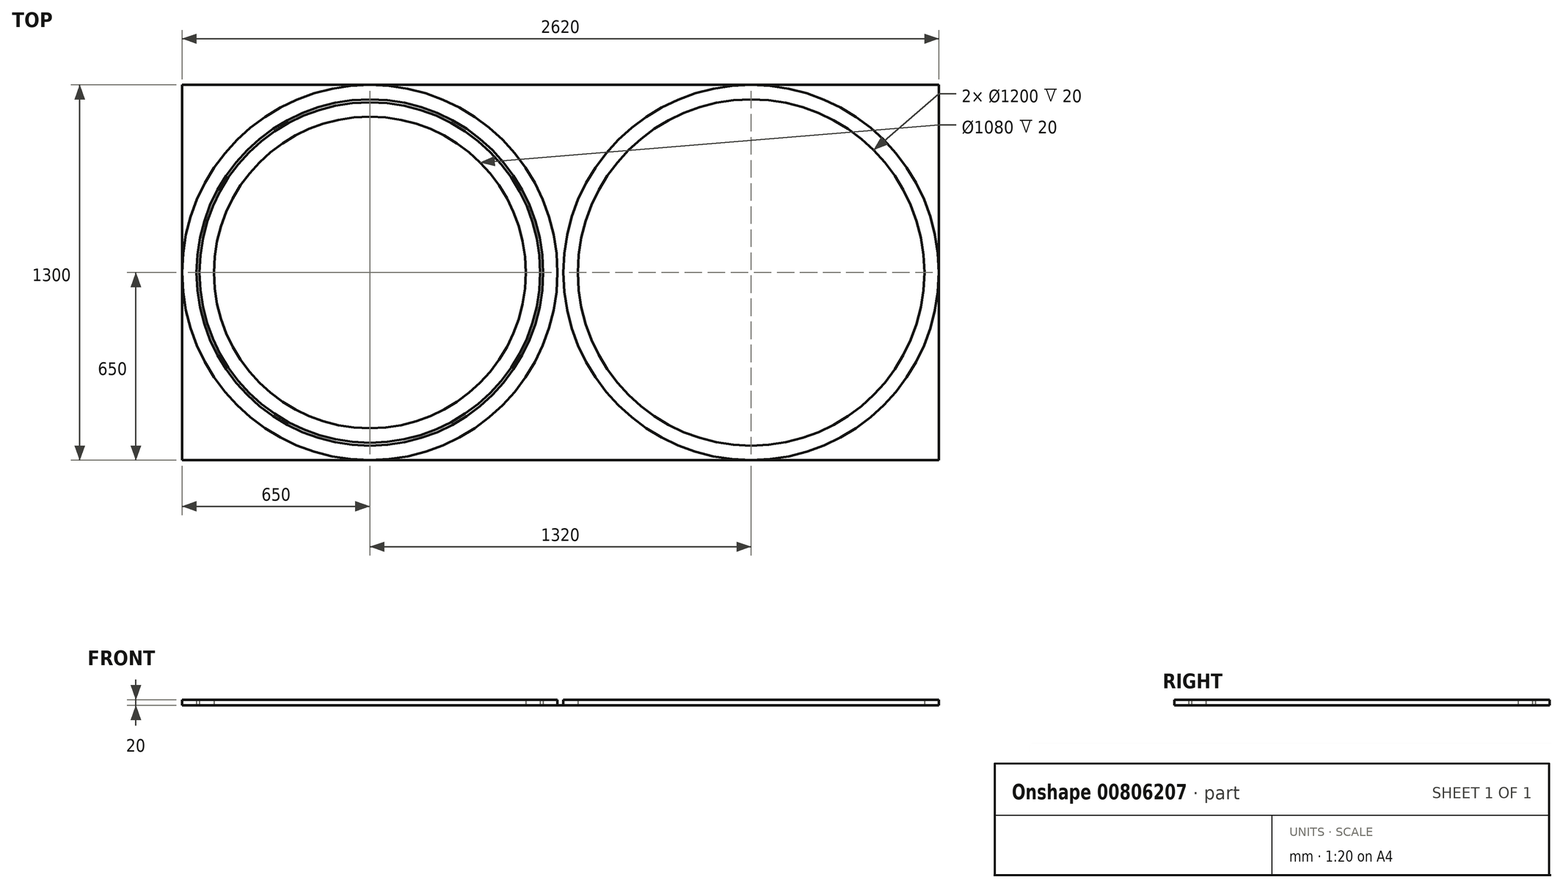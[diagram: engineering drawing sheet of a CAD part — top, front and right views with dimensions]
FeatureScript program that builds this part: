
annotation { "Feature Type Name" : "Feature", "Feature Type Description" : "" }
export const myFeature = defineFeature(function(context is Context, id is Id, definition is map)
    precondition{}
    {
        {
            var Q0;
            Q0=qCreatedBy(makeId("Top.planeOp"),FACE);
            var sketch = newSketch(context, id + "F0", { "sketchPlane" : qUnion([Q0])});
            skLineSegment(sketch, "E0.bottom", {"start": v(1310, -650) * mm, "end": v(-1310, -650) * mm});
            skLineSegment(sketch, "E0.top", {"start": v(1310, 650) * mm, "end": v(-1310, 650) * mm});
            skLineSegment(sketch, "E0.left", {"start": v(1310, -650) * mm, "end": v(1310, 650) * mm});
            skLineSegment(sketch, "E0.right", {"start": v(-1310, -650) * mm, "end": v(-1310, 650) * mm});
            skPoint(sketch, "E0.middle", {"position": v(0, 0) * mm});
            skLineSegment(sketch, "E1", {"start": v(-1310, -650) * mm, "end": v(-1310, 0) * mm});
            skLineSegment(sketch, "E2", {"start": v(-1310, 0) * mm, "end": v(-660, 0) * mm});
            skCircle(sketch, "E3", {"center": v(-660, 0) * mm, "radius": 650 * mm});
            skCircle(sketch, "E4", {"center": v(-660, 0) * mm, "radius": 600 * mm});
            skCircle(sketch, "E5", {"center": v(-660, 0) * mm, "radius": 590 * mm});
            skCircle(sketch, "E6", {"center": v(-660, 0) * mm, "radius": 540 * mm});
            skLineSegment(sketch, "E7", {"start": v(-660, 0) * mm, "end": v(660, 0) * mm});
            skCircle(sketch, "E8", {"center": v(660, 0) * mm, "radius": 650 * mm});
            skCircle(sketch, "E9", {"center": v(660, 0) * mm, "radius": 600 * mm});
            skSolve(sketch);
        }
        {
            var Q0;
            {var subQ5=sQuery(id+"F0.wireOp",EDGE,"E3");var subQ6=makeQuery(id+"F0.imprint","INTERSECT",VERTEX,{"derivedFrom":[sQuery(id+"F0.wireOp",EDGE,"E0.bottom"),subQ5]});Q0=makeQuery(id+"F0.imprint","IMPRINT",FACE,{"disambiguationData":[TD([[makeQuery(id+"F0.imprint","IMPRINT",EDGE,{"disambiguationData":[TD([[subQ6,-1.0]])],"derivedFrom":subQ5}),1.0]])]});}
            var Q1;
            {var subQ5=sQuery(id+"F0.wireOp",EDGE,"E3");var subQ6=makeQuery(id+"F0.imprint","INTERSECT",VERTEX,{"derivedFrom":[sQuery(id+"F0.wireOp",EDGE,"E0.top"),subQ5]});Q1=makeQuery(id+"F0.imprint","IMPRINT",FACE,{"disambiguationData":[TD([[makeQuery(id+"F0.imprint","IMPRINT",EDGE,{"disambiguationData":[TD([[subQ6,1.0]])],"derivedFrom":subQ5}),1.0]])]});}
            var Q2;
            Q2=makeQuery(id+"F0.imprint","IMPRINT",FACE,{"disambiguationData":[TD([[makeQuery(id+"F0.imprint","IMPRINT",EDGE,{"derivedFrom":sQuery(id+"F0.wireOp",EDGE,"E9")}),-1.0]])]});
            extrude(context, id + "F1", {"entities" : qUnion([Q0, Q1, Q2]), "depth" : 20 * mm, "offsetDistance" : 25 * mm});
        }
        {
            var Q0;
            {var subQ0=sQuery(id+"F0.wireOp",EDGE,"E5");var subQ1=sQuery(id+"F0.wireOp",EDGE,"E2");var subQ2=makeQuery(id+"F0.imprint","INTERSECT",VERTEX,{"derivedFrom":[subQ1,subQ0]});Q0=makeQuery(id+"F0.imprint","IMPRINT",FACE,{"disambiguationData":[TD([[makeQuery(id+"F0.imprint","IMPRINT",EDGE,{"disambiguationData":[TD([[subQ2,-1.0]])],"derivedFrom":subQ1}),1.0]])]});}
            var Q1;
            {var subQ0=sQuery(id+"F0.wireOp",EDGE,"E5");var subQ1=sQuery(id+"F0.wireOp",EDGE,"E2");var subQ2=makeQuery(id+"F0.imprint","INTERSECT",VERTEX,{"derivedFrom":[subQ1,subQ0]});Q1=makeQuery(id+"F0.imprint","IMPRINT",FACE,{"disambiguationData":[TD([[makeQuery(id+"F0.imprint","IMPRINT",EDGE,{"disambiguationData":[TD([[subQ2,-1.0]])],"derivedFrom":subQ1}),-1.0]])]});}
            var Q2;
            Q2=sQuery(id+"F0.wireOp",EDGE,"E6");
            var Q3;
            Q3=sQuery(id+"F0.wireOp",EDGE,"E5");
            extrude(context, id + "F2", {"entities" : qUnion([Q0, Q1]), "surfaceEntities" : qUnion([Q2, Q3]), "depth" : 20 * mm, "offsetDistance" : 25 * mm});
        }
        {
            var Q0;
            {var subQ0=sQuery(id+"F0.wireOp",EDGE,"E0.right");Q0=makeQuery(id+"F0.imprint","IMPRINT",FACE,{"disambiguationData":[TD([[makeQuery(id+"F0.imprint","IMPRINT",EDGE,{"derivedFrom":subQ0}),-1.0]])]});}
            var Q1;
            {var subQ0=sQuery(id+"F0.wireOp",EDGE,"E8");var subQ1=sQuery(id+"F0.wireOp",EDGE,"E0.top");var subQ2=makeQuery(id+"F0.imprint","INTERSECT",VERTEX,{"derivedFrom":[subQ1,subQ0]});Q1=makeQuery(id+"F0.imprint","IMPRINT",FACE,{"disambiguationData":[TD([[makeQuery(id+"F0.imprint","IMPRINT",EDGE,{"disambiguationData":[TD([[subQ2,-1.0]])],"derivedFrom":subQ1}),1.0]])]});}
            var Q2;
            {var subQ0=sQuery(id+"F0.wireOp",EDGE,"E8");var subQ1=sQuery(id+"F0.wireOp",EDGE,"E0.bottom");var subQ2=makeQuery(id+"F0.imprint","INTERSECT",VERTEX,{"derivedFrom":[subQ1,subQ0]});Q2=makeQuery(id+"F0.imprint","IMPRINT",FACE,{"disambiguationData":[TD([[makeQuery(id+"F0.imprint","IMPRINT",EDGE,{"disambiguationData":[TD([[subQ2,-1.0]])],"derivedFrom":subQ1}),-1.0]])]});}
            var Q3;
            {var subQ0=sQuery(id+"F0.wireOp",EDGE,"E1");Q3=makeQuery(id+"F0.imprint","IMPRINT",FACE,{"disambiguationData":[TD([[makeQuery(id+"F0.imprint","IMPRINT",EDGE,{"derivedFrom":subQ0}),-1.0]])]});}
            var Q4;
            {var subQ0=sQuery(id+"F0.wireOp",EDGE,"E0.left");var subQ1=sQuery(id+"F0.wireOp",EDGE,"E0.bottom");var subQ2=makeQuery(id+"F0.imprint","INTERSECT",VERTEX,{"derivedFrom":[subQ1,subQ0]});Q4=makeQuery(id+"F0.imprint","IMPRINT",FACE,{"disambiguationData":[TD([[makeQuery(id+"F0.imprint","IMPRINT",EDGE,{"disambiguationData":[TD([[subQ2,-1.0]])],"derivedFrom":subQ1}),-1.0]])]});}
            var Q5;
            {var subQ0=sQuery(id+"F0.wireOp",EDGE,"E0.left");var subQ1=sQuery(id+"F0.wireOp",EDGE,"E0.top");var subQ2=makeQuery(id+"F0.imprint","INTERSECT",VERTEX,{"derivedFrom":[subQ1,subQ0]});Q5=makeQuery(id+"F0.imprint","IMPRINT",FACE,{"disambiguationData":[TD([[makeQuery(id+"F0.imprint","IMPRINT",EDGE,{"disambiguationData":[TD([[subQ2,-1.0]])],"derivedFrom":subQ1}),1.0]])]});}
            var Q6;
            {var subQ0=sQuery(id+"F0.wireOp",EDGE,"E7");var subQ1=sQuery(id+"F0.wireOp",EDGE,"E2");var subQ2=makeQuery(id+"F0.imprint","INTERSECT",VERTEX,{"derivedFrom":[subQ1,subQ0]});Q6=makeQuery(id+"F0.imprint","IMPRINT",FACE,{"disambiguationData":[TD([[makeQuery(id+"F0.imprint","IMPRINT",EDGE,{"disambiguationData":[TD([[subQ2,1.0]])],"derivedFrom":subQ1}),1.0]])]});}
            var Q7;
            {var subQ0=sQuery(id+"F0.wireOp",EDGE,"E7");var subQ1=sQuery(id+"F0.wireOp",EDGE,"E2");var subQ2=makeQuery(id+"F0.imprint","INTERSECT",VERTEX,{"derivedFrom":[subQ1,subQ0]});Q7=makeQuery(id+"F0.imprint","IMPRINT",FACE,{"disambiguationData":[TD([[makeQuery(id+"F0.imprint","IMPRINT",EDGE,{"disambiguationData":[TD([[subQ2,1.0]])],"derivedFrom":subQ1}),-1.0]])]});}
            var Q8;
            Q8=makeQuery(id+"F0.imprint","IMPRINT",FACE,{"disambiguationData":[TD([[makeQuery(id+"F0.imprint","IMPRINT",EDGE,{"derivedFrom":sQuery(id+"F0.wireOp",EDGE,"E9")}),1.0]])]});
            extrude(context, id + "F3", {"entities" : qUnion([Q0, Q1, Q2, Q3, Q4, Q5, Q6, Q7, Q8]), "depth" : 1 * mm, "offsetDistance" : 25 * mm});
        }
    });
